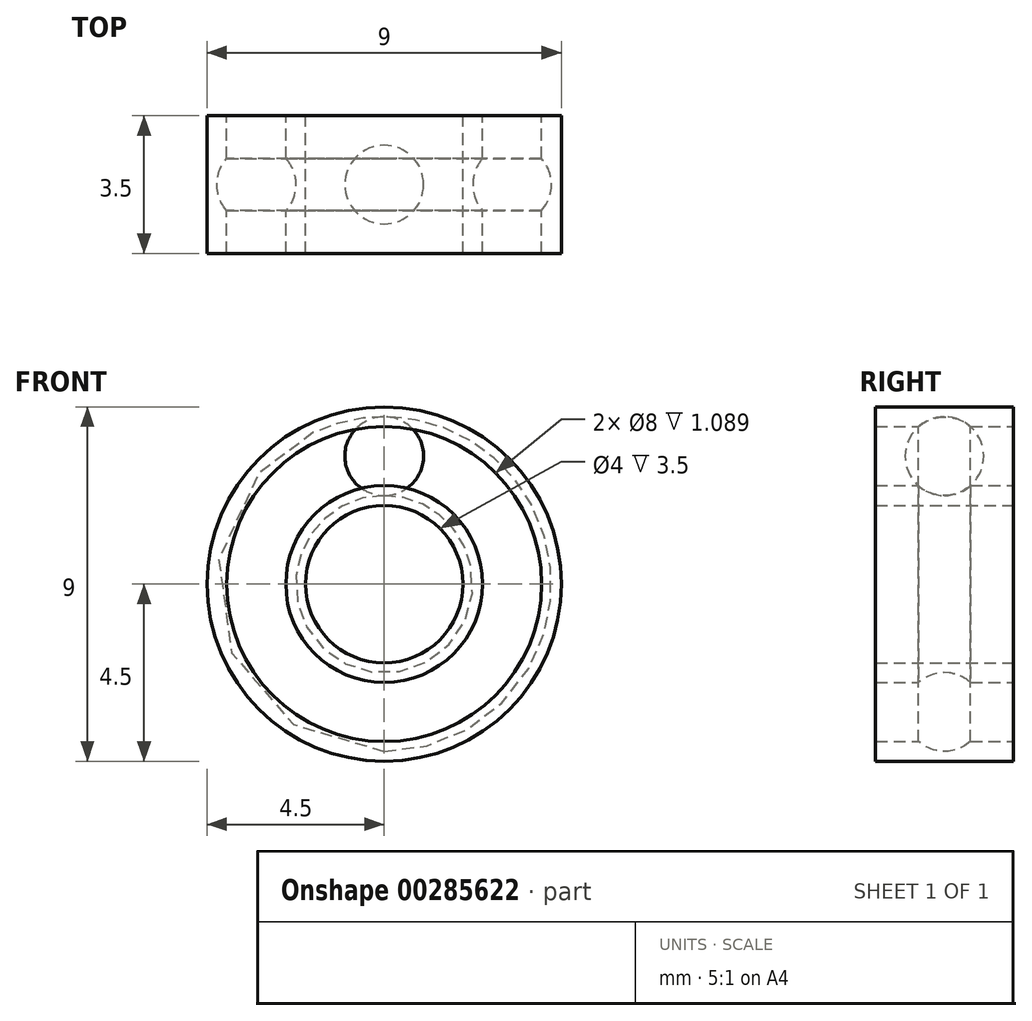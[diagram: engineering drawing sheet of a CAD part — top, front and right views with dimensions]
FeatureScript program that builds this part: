
annotation { "Feature Type Name" : "Feature", "Feature Type Description" : "" }
export const myFeature = defineFeature(function(context is Context, id is Id, definition is map)
    precondition{}
    {
        {
            var Q0;
            Q0=qCreatedBy(makeId("Front.planeOp"),FACE);
            var sketch = newSketch(context, id + "F0", { "sketchPlane" : qUnion([Q0])});
            skCircle(sketch, "E0", {"center": v(0, 0) * mm, "radius": 2 * mm});
            skCircle(sketch, "E1", {"center": v(0, 0) * mm, "radius": 2.5 * mm});
            skCircle(sketch, "E2", {"center": v(0, 0) * mm, "radius": 4 * mm});
            skCircle(sketch, "E3", {"center": v(0, 0) * mm, "radius": 4.5 * mm});
            skCircle(sketch, "E4", {"center": v(0, 0) * mm, "radius": 3.25 * mm, "construction": true});
            skLineSegment(sketch, "E5", {"start": v(0, 5.53) * mm, "end": v(0, -5.5) * mm, "construction": true});
            skArc(sketch, "E6", {"start": v(0, 2.25) * mm, "mid": v(1, 3.25) * mm, "end": v(0, 4.25) * mm});
            skLineSegment(sketch, "E7", {"start": v(0, 4.25) * mm, "end": v(0, 2.25) * mm});
            skLineSegment(sketch, "E8", {"start": v(0, 3.25) * mm, "end": v(0, 4.25) * mm, "construction": true});
            skArc(sketch, "E9", {"start": v(0, 2.25) * mm, "mid": v(-1, 3.25) * mm, "end": v(0, 4.25) * mm, "construction": true});
            skSolve(sketch);
        }
        {
            var Q0;
            Q0=makeQuery(id+"F0.imprint","IMPRINT",FACE,{"disambiguationData":[TD([[makeQuery(id+"F0.imprint","IMPRINT",EDGE,{"derivedFrom":sQuery(id+"F0.wireOp",EDGE,"E0")}),-1.0]])]});
            var Q1;
            {var subQ0=sQuery(id+"F0.wireOp",EDGE,"P58FV9AN-sAPW-c1iF-Mfc2-iSeX3mTv5IeI");var subQ1=sQuery(id+"F0.wireOp",EDGE,"E1");var subQ2=makeQuery(id+"F0.imprint","INTERSECT",VERTEX,{"derivedFrom":[subQ1,subQ0]});Q1=makeQuery(id+"F0.imprint","IMPRINT",FACE,{"disambiguationData":[TD([[makeQuery(id+"F0.imprint","IMPRINT",EDGE,{"disambiguationData":[TD([[subQ2,-1.0]])],"derivedFrom":subQ1}),1.0]])]});}
            extrude(context, id + "F1", {"entities" : qUnion([Q0, Q1]), "endBound" : BoundingType.SYMMETRIC, "depth" : 3.5 * mm});
        }
        {
            var Q0;
            Q0=makeQuery(id+"F0.imprint","IMPRINT",FACE,{"disambiguationData":[TD([[makeQuery(id+"F0.imprint","IMPRINT",EDGE,{"derivedFrom":sQuery(id+"F0.wireOp",EDGE,"E3")}),1.0]])]});
            var Q1;
            {var subQ0=sQuery(id+"F0.wireOp",EDGE,"P58FV9AN-sAPW-c1iF-Mfc2-iSeX3mTv5IeI");var subQ1=sQuery(id+"F0.wireOp",EDGE,"E2");var subQ2=makeQuery(id+"F0.imprint","INTERSECT",VERTEX,{"derivedFrom":[subQ1,subQ0]});Q1=makeQuery(id+"F0.imprint","IMPRINT",FACE,{"disambiguationData":[TD([[makeQuery(id+"F0.imprint","IMPRINT",EDGE,{"disambiguationData":[TD([[subQ2,-1.0]])],"derivedFrom":subQ1}),-1.0]])]});}
            extrude(context, id + "F2", {"entities" : qUnion([Q0, Q1]), "operationType" : NewBodyOperationType.ADD, "endBound" : BoundingType.SYMMETRIC, "depth" : 3.5 * mm});
        }
        {
            var Q0;
            Q0=qCreatedBy(makeId("Right.planeOp"),FACE);
            var sketch = newSketch(context, id + "F3", { "sketchPlane" : qUnion([Q0])});
            skLineSegment(sketch, "E10", {"start": v(-0.66, 2.5) * mm, "end": v(0.66, 2.5) * mm});
            skArc(sketch, "E11", {"start": v(-0.66, 2.5) * mm, "mid": v(0, 2.25) * mm, "end": v(0.66, 2.5) * mm});
            skLineSegment(sketch, "E12", {"start": v(1.2, 3.25) * mm, "end": v(-1.17, 3.25) * mm, "construction": true});
            skLineSegment(sketch, "E13.MirrorCS", {"start": v(-0.66, 4) * mm, "end": v(0.66, 4) * mm});
            skArc(sketch, "E14.MirrorCS", {"start": v(-0.66, 4) * mm, "mid": v(0, 4.25) * mm, "end": v(0.66, 4) * mm});
            skLineSegment(sketch, "E15", {"start": v(0, 0) * mm, "end": v(0, 5.41) * mm, "construction": true});
            skSolve(sketch);
        }
        {
            var Q0;
            Q0=makeQuery(id+"F3.imprint","IMPRINT",FACE,{"disambiguationData":[TD([[makeQuery(id+"F3.imprint","IMPRINT",EDGE,{"derivedFrom":sQuery(id+"F3.wireOp",EDGE,"E10")}),-1.0]])]});
            var Q1;
            Q1=sQuery(id+"F0.wireOp",EDGE,"E0");
            revolve(context, id + "F4", {"operationType" : NewBodyOperationType.REMOVE, "entities" : qUnion([Q0]), "axis" : qUnion([Q1]), "revolveType" : RevolveType.FULL});
        }
        {
            var Q0;
            Q0=makeQuery(id+"F3.imprint","IMPRINT",FACE,{"disambiguationData":[TD([[makeQuery(id+"F3.imprint","IMPRINT",EDGE,{"derivedFrom":sQuery(id+"F3.wireOp",EDGE,"E13.MirrorCS")}),1.0]])]});
            var Q1;
            Q1=sQuery(id+"F0.wireOp",EDGE,"E4");
            revolve(context, id + "F5", {"operationType" : NewBodyOperationType.REMOVE, "entities" : qUnion([Q0]), "axis" : qUnion([Q1]), "revolveType" : RevolveType.FULL, "oppositeDirection" : true});
        }
        {
            var Q0;
            {var subQ0=sQuery(id+"F0.wireOp",EDGE,"E6");var subQ1=sQuery(id+"F0.wireOp",EDGE,"E2");var subQ2=makeQuery(id+"F0.imprint","INTERSECT",VERTEX,{"derivedFrom":[subQ1,subQ0]});Q0=makeQuery(id+"F0.imprint","IMPRINT",FACE,{"disambiguationData":[TD([[makeQuery(id+"F0.imprint","IMPRINT",EDGE,{"disambiguationData":[TD([[subQ2,-1.0]])],"derivedFrom":subQ1}),-1.0]])]});}
            var Q1;
            {var subQ0=sQuery(id+"F0.wireOp",EDGE,"E6");var subQ1=sQuery(id+"F0.wireOp",EDGE,"E1");var subQ2=makeQuery(id+"F0.imprint","INTERSECT",VERTEX,{"derivedFrom":[subQ1,subQ0]});Q1=makeQuery(id+"F0.imprint","IMPRINT",FACE,{"disambiguationData":[TD([[makeQuery(id+"F0.imprint","IMPRINT",EDGE,{"disambiguationData":[TD([[subQ2,-1.0]])],"derivedFrom":subQ1}),-1.0]])]});}
            var Q2;
            {var subQ0=sQuery(id+"F0.wireOp",EDGE,"E6");var subQ1=sQuery(id+"F0.wireOp",EDGE,"E1");var subQ2=makeQuery(id+"F0.imprint","INTERSECT",VERTEX,{"derivedFrom":[subQ1,subQ0]});Q2=makeQuery(id+"F0.imprint","IMPRINT",FACE,{"disambiguationData":[TD([[makeQuery(id+"F0.imprint","IMPRINT",EDGE,{"disambiguationData":[TD([[subQ2,-1.0]])],"derivedFrom":subQ1}),1.0]])]});}
            var Q3;
            Q3=sQuery(id+"F0.wireOp",EDGE,"E5");
            revolve(context, id + "F6", {"entities" : qUnion([Q0, Q1, Q2]), "axis" : qUnion([Q3]), "revolveType" : RevolveType.FULL});
        }
    });
